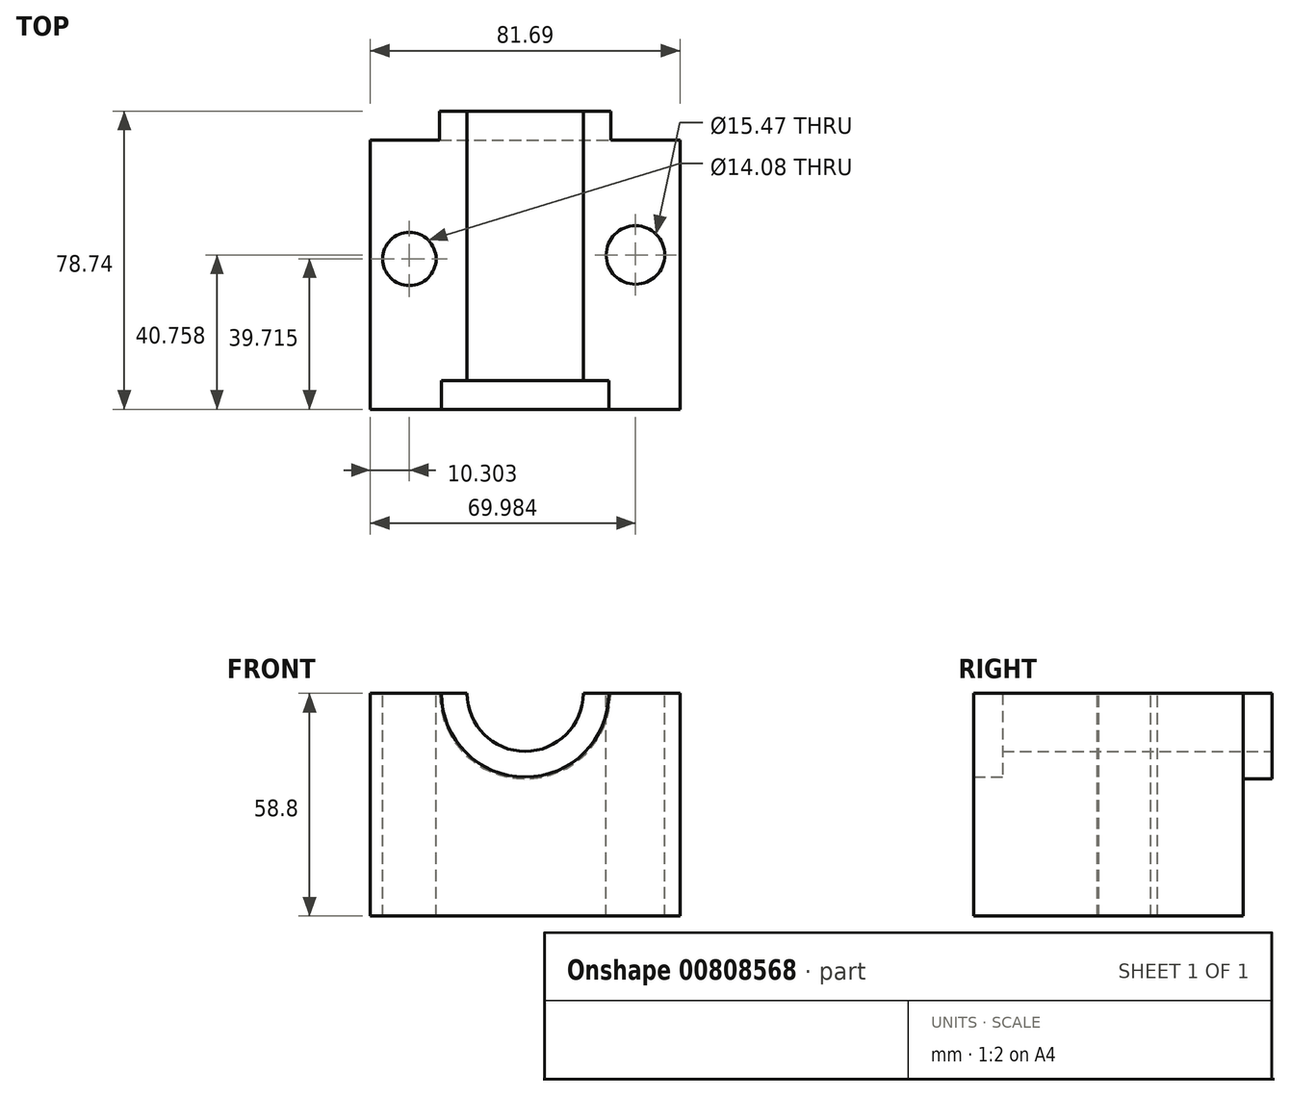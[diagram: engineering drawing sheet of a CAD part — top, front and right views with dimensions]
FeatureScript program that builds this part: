
annotation { "Feature Type Name" : "Feature", "Feature Type Description" : "" }
export const myFeature = defineFeature(function(context is Context, id is Id, definition is map)
    precondition{}
    {
        {
            var Q0;
            Q0=qCreatedBy(makeId("Front.planeOp"),FACE);
            var sketch = newSketch(context, id + "F0", { "sketchPlane" : qUnion([Q0])});
            skLineSegment(sketch, "E0.bottom", {"start": v(-30.24, 32.65) * mm, "end": v(-4.72, 32.65) * mm});
            skLineSegment(sketch, "E0.top", {"start": v(-30.24, -26.15) * mm, "end": v(51.45, -26.15) * mm});
            skLineSegment(sketch, "E0.left", {"start": v(-30.24, 32.65) * mm, "end": v(-30.24, -26.15) * mm});
            skLineSegment(sketch, "E0.right", {"start": v(51.45, 32.65) * mm, "end": v(51.45, -26.15) * mm});
            skArc(sketch, "E1", {"start": v(-11.98, 32.65) * mm, "mid": v(10.6, 10.07) * mm, "end": v(33.19, 32.65) * mm});
            skArc(sketch, "E2", {"start": v(-4.72, 32.65) * mm, "mid": v(10.6, 17.33) * mm, "end": v(25.93, 32.65) * mm});
            skLineSegment(sketch, "E3.trimOffspring", {"start": v(25.93, 32.65) * mm, "end": v(51.45, 32.65) * mm});
            skSolve(sketch);
        }
        {
            var Q0;
            Q0 = qSketchRegion(id + "F0", true);
            extrude(context, id + "F1", {"entities" : qUnion([Q0]), "depth" : 63.5 * mm, "offsetDistance" : 25.4 * mm});
        }
        {
            var Q0;
            {var subQ2=sQuery(id+"F0.wireOp",EDGE,"E1");Q0=makeQuery(id+"F0.imprint","IMPRINT",FACE,{"disambiguationData":[TD([[makeQuery(id+"F0.imprint","IMPRINT",EDGE,{"derivedFrom":subQ2}),1.0]])]});}
            extrude(context, id + "F2", {"entities" : qUnion([Q0]), "operationType" : NewBodyOperationType.ADD, "oppositeDirection" : true, "depth" : 7.62 * mm, "offsetDistance" : 25.4 * mm});
        }
        {
            var Q0;
            Q0=makeQuery(id+"F1.opExtrude","CAP_FACE",FACE,{"disambiguationData":[OSD([sQuery(id+"F0.wireOp",EDGE,"E0.bottom"),sQuery(id+"F0.wireOp",EDGE,"E0.top"),sQuery(id+"F0.wireOp",EDGE,"E0.left"),sQuery(id+"F0.wireOp",EDGE,"E0.right"),sQuery(id+"F0.wireOp",EDGE,"E2"),sQuery(id+"F0.wireOp",EDGE,"E3.trimOffspring")])],"isStart":false});
            var sketch = newSketch(context, id + "F3", { "sketchPlane" : qUnion([Q0])});
            skArc(sketch, "E4", {"start": v(32.7, 32.65) * mm, "mid": v(10.6, 10.55) * mm, "end": v(-11.5, 32.65) * mm});
            skSolve(sketch);
        }
        {
            var Q0;
            Q0 = qSketchRegion(id + "F3", true);
            var Q1;
            {var subQ0=sQuery(id+"F3.wireOp",EDGE,"E4");Q1=makeQuery(id+"F3.imprint","IMPRINT",FACE,{"disambiguationData":[TD([[makeQuery(id+"F3.imprint","IMPRINT",EDGE,{"derivedFrom":subQ0}),-1.0]])]});}
            extrude(context, id + "F4", {"entities" : qUnion([Q0, Q1]), "operationType" : NewBodyOperationType.ADD, "depth" : 7.62 * mm, "offsetDistance" : 25.4 * mm});
        }
        {
            var Q0;
            {var subQ0=sQuery(id+"F0.wireOp",EDGE,"E0.bottom");Q0=makeQuery(id+"F4.boolean.opBoolean","MERGE",FACE,{"derivedFrom":[makeQuery(id+"F2.boolean.opBoolean","MERGE",FACE,{"derivedFrom":[makeQuery(id+"F1.opExtrude","SWEPT_FACE",FACE,{"disambiguationData":[OSD([subQ0])]}),makeQuery(id+"F2.opExtrude","SWEPT_FACE",FACE,{"disambiguationData":[OSD([subQ0])]})]}),makeQuery(id+"F4.opExtrude","SWEPT_FACE",FACE,{"disambiguationData":[OSD([subQ0])]})]});}
            var sketch = newSketch(context, id + "F5", { "sketchPlane" : qUnion([Q0])});
            skCircle(sketch, "E5", {"center": v(-19.94, -31.4) * mm, "radius": 7.04 * mm});
            skCircle(sketch, "E6", {"center": v(39.74, -30.36) * mm, "radius": 7.74 * mm});
            skSolve(sketch);
        }
        {
            var Q0;
            Q0=makeQuery(id+"F5.imprint","IMPRINT",FACE,{"disambiguationData":[TD([[makeQuery(id+"F5.imprint","IMPRINT",EDGE,{"derivedFrom":sQuery(id+"F5.wireOp",EDGE,"E6")}),1.0]])]});
            extrude(context, id + "F6", {"entities" : qUnion([Q0]), "operationType" : NewBodyOperationType.REMOVE, "oppositeDirection" : true, "depth" : 73.15 * mm, "offsetDistance" : 25.4 * mm});
        }
        {
            var Q0;
            Q0 = qSketchRegion(id + "F5", true);
            extrude(context, id + "F7", {"entities" : qUnion([Q0]), "operationType" : NewBodyOperationType.REMOVE, "oppositeDirection" : true, "depth" : 76.2 * mm, "offsetDistance" : 25.4 * mm});
        }
    });
